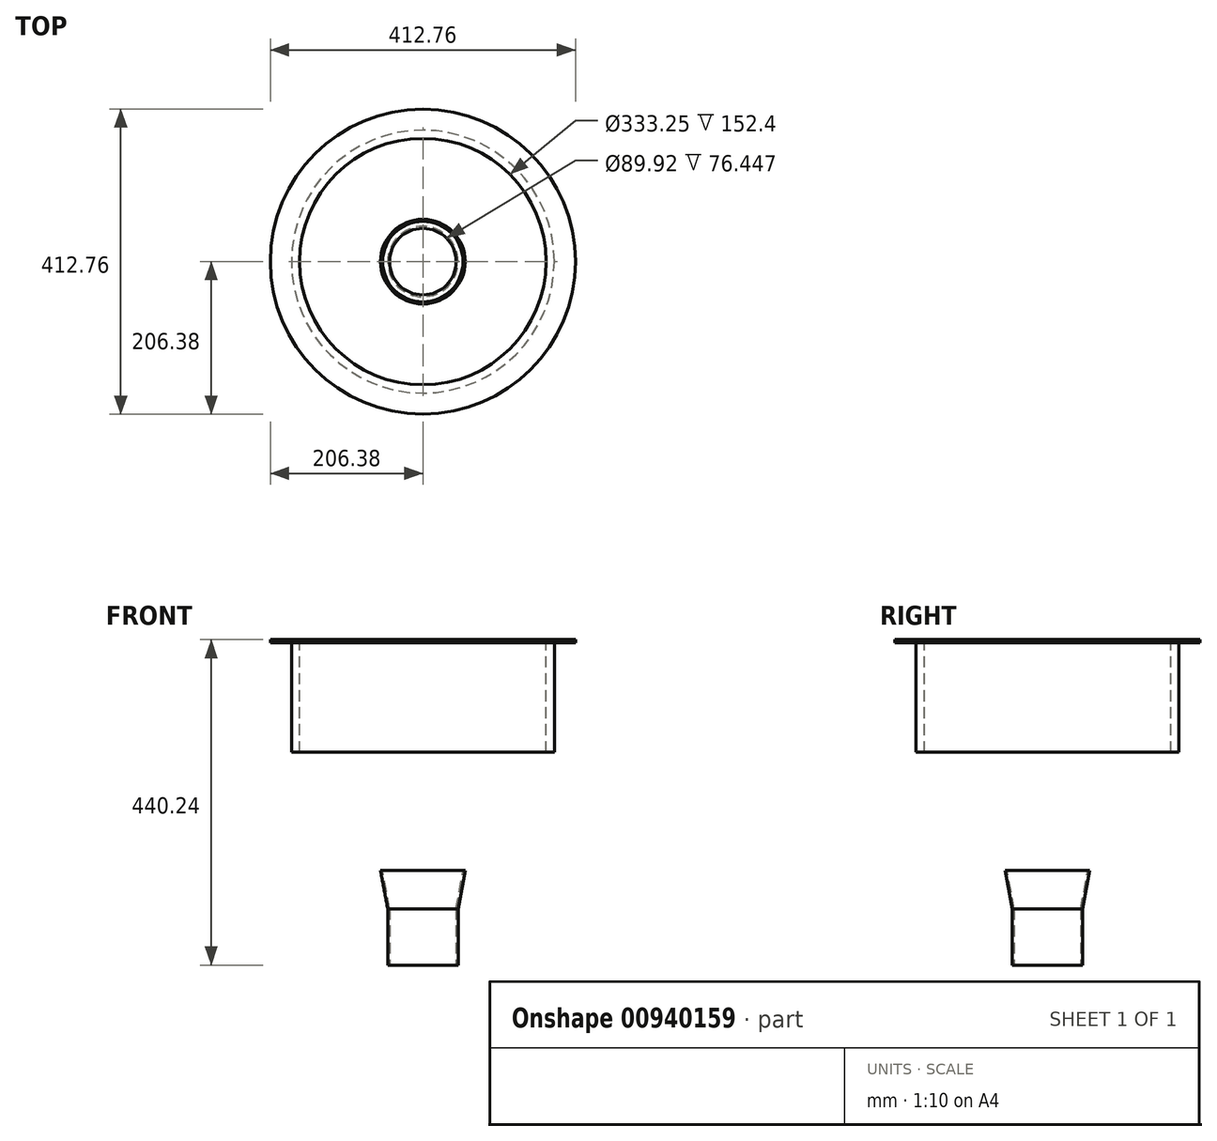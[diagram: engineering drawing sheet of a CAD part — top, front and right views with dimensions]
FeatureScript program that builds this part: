
annotation { "Feature Type Name" : "Feature", "Feature Type Description" : "" }
export const myFeature = defineFeature(function(context is Context, id is Id, definition is map)
    precondition{}
    {
        {
            var Q0;
            Q0=qCreatedBy(makeId("Top.planeOp"),FACE);
            var sketch = newSketch(context, id + "F0", { "sketchPlane" : qUnion([Q0])});
            skCircle(sketch, "E0", {"center": v(0, 0) * mm, "radius": 166.62 * mm});
            skCircle(sketch, "E1", {"center": v(0, 0) * mm, "radius": 177.8 * mm});
            skSolve(sketch);
        }
        {
            var Q0;
            Q0=qCreatedBy(makeId("Front.planeOp"),FACE);
            var sketch = newSketch(context, id + "F1", { "sketchPlane" : qUnion([Q0])});
            skLineSegment(sketch, "E2", {"start": v(0, 0) * mm, "end": v(0, -165.1) * mm, "construction": true});
            skLineSegment(sketch, "E3", {"start": v(-177.8, -71.37) * mm, "end": v(-177.8, 0) * mm});
            skLineSegment(sketch, "E4", {"start": v(-177.8, 0) * mm, "end": v(0, 0) * mm, "construction": true});
            skEllipticalArc(sketch, "E5", {});
            skLineSegment(sketch, "E6", {"start": v(0, -71.37) * mm, "end": v(-177.8, -71.37) * mm, "construction": true});
            skLineSegment(sketch, "E7.0", {"start": v(-166.62, -71.37) * mm, "end": v(-166.62, 0) * mm});
            skFitSpline(sketch, "E7.1", {"points": [v(166.62, -72.28) * mm, v(166.63, -71.37) * mm, v(166.62, -70.47) * mm, v(166.57, -69.27) * mm, v(166.47, -67.77) * mm, v(166.26, -65.98) * mm, v(165.86, -63.58) * mm, v(165.16, -60.58) * mm, v(163.96, -56.97) * mm, v(162.41, -53.34) * mm, v(160.5, -49.7) * mm, v(158.2, -46.05) * mm, v(155.54, -42.4) * mm, v(152.5, -38.78) * mm, v(149.06, -35.18) * mm, v(145.25, -31.63) * mm, v(141.06, -28.13) * mm, v(137.25, -25.27) * mm, v(134.02, -23.03) * mm, v(131.5, -21.37) * mm, v(128.9, -19.73) * mm, v(126.65, -18.39) * mm, v(124.8, -17.33) * mm, v(123.4, -16.54) * mm, v(122.2, -15.89) * mm, v(121.24, -15.37) * mm, v(120.51, -14.99) * mm, v(119.78, -14.6) * mm, v(118.8, -14.1) * mm, v(117.56, -13.46) * mm, v(116.05, -12.72) * mm, v(114.02, -11.73) * mm, v(111.43, -10.53) * mm, v(108.26, -9.13) * mm, v(105.03, -7.76) * mm, v(100.63, -6) * mm, v(94.98, -3.9) * mm, v(87.96, -1.57) * mm, v(80.73, 0.58) * mm, v(73.3, 2.55) * mm, v(65.68, 4.33) * mm, v(57.9, 5.91) * mm, v(49.96, 7.3) * mm, v(41.9, 8.48) * mm, v(33.7, 9.45) * mm, v(26.78, 10.1) * mm, v(21.2, 10.5) * mm, v(17, 10.74) * mm, v(12.77, 10.94) * mm, v(9.23, 11.05) * mm, v(6.4, 11.12) * mm, v(4.27, 11.15) * mm, v(2.5, 11.17) * mm, v(1.07, 11.17) * mm, v(0, 11.18) * mm, v(-1.07, 11.17) * mm, v(-2.5, 11.17) * mm, v(-4.27, 11.15) * mm, v(-6.4, 11.12) * mm, v(-9.23, 11.05) * mm, v(-12.77, 10.94) * mm, v(-17, 10.74) * mm, v(-21.2, 10.5) * mm, v(-26.78, 10.1) * mm, v(-33.7, 9.45) * mm, v(-41.9, 8.48) * mm, v(-49.96, 7.3) * mm, v(-57.9, 5.91) * mm, v(-65.68, 4.33) * mm, v(-73.3, 2.55) * mm, v(-80.73, 0.58) * mm, v(-87.96, -1.57) * mm, v(-94.98, -3.9) * mm, v(-100.63, -6) * mm, v(-105.03, -7.76) * mm, v(-108.26, -9.13) * mm, v(-111.43, -10.53) * mm, v(-114.02, -11.73) * mm, v(-116.05, -12.72) * mm, v(-117.56, -13.46) * mm, v(-118.8, -14.1) * mm, v(-119.78, -14.6) * mm, v(-120.51, -14.99) * mm, v(-121.24, -15.37) * mm, v(-122.2, -15.89) * mm, v(-123.4, -16.54) * mm, v(-124.8, -17.33) * mm, v(-126.65, -18.39) * mm, v(-128.9, -19.73) * mm, v(-131.5, -21.37) * mm, v(-134.02, -23.03) * mm, v(-137.25, -25.27) * mm, v(-141.06, -28.13) * mm, v(-145.25, -31.63) * mm, v(-149.06, -35.18) * mm, v(-152.5, -38.78) * mm, v(-155.54, -42.4) * mm, v(-158.2, -46.05) * mm, v(-160.5, -49.7) * mm, v(-162.41, -53.34) * mm, v(-163.96, -56.97) * mm, v(-165.16, -60.58) * mm, v(-165.86, -63.58) * mm, v(-166.26, -65.98) * mm, v(-166.47, -67.77) * mm, v(-166.57, -69.27) * mm, v(-166.62, -70.47) * mm, v(-166.63, -71.37) * mm, v(-166.62, -72.28) * mm, v(-166.57, -73.48) * mm, v(-166.47, -74.97) * mm, v(-166.26, -76.77) * mm, v(-165.86, -79.17) * mm, v(-165.16, -82.17) * mm, v(-163.96, -85.78) * mm, v(-162.41, -89.4) * mm, v(-160.5, -93.05) * mm, v(-158.2, -96.7) * mm, v(-155.54, -100.34) * mm, v(-152.5, -103.97) * mm, v(-149.06, -107.56) * mm, v(-145.25, -111.12) * mm, v(-141.06, -114.62) * mm, v(-137.25, -117.47) * mm, v(-134.02, -119.72) * mm, v(-131.5, -121.38) * mm, v(-128.9, -123.02) * mm, v(-126.65, -124.36) * mm, v(-124.8, -125.42) * mm, v(-123.4, -126.2) * mm, v(-122.2, -126.86) * mm, v(-121.24, -127.38) * mm, v(-120.51, -127.76) * mm, v(-119.78, -128.15) * mm, v(-118.8, -128.66) * mm, v(-117.56, -129.29) * mm, v(-116.05, -130.03) * mm, v(-114.02, -131.01) * mm, v(-111.43, -132.22) * mm, v(-108.26, -133.62) * mm, v(-105.03, -134.98) * mm, v(-100.63, -136.74) * mm, v(-94.98, -138.84) * mm, v(-87.96, -141.18) * mm, v(-80.73, -143.33) * mm, v(-73.3, -145.3) * mm, v(-65.68, -147.08) * mm, v(-57.9, -148.66) * mm, v(-49.96, -150.05) * mm, v(-41.9, -151.23) * mm, v(-33.7, -152.2) * mm, v(-26.78, -152.84) * mm, v(-21.2, -153.24) * mm, v(-17, -153.49) * mm, v(-12.77, -153.68) * mm, v(-9.23, -153.8) * mm, v(-6.4, -153.86) * mm, v(-4.27, -153.9) * mm, v(-2.5, -153.92) * mm, v(-1.07, -153.92) * mm, v(0, -153.92) * mm, v(1.07, -153.92) * mm, v(2.5, -153.92) * mm, v(4.27, -153.9) * mm, v(6.4, -153.86) * mm, v(9.23, -153.8) * mm, v(12.77, -153.68) * mm, v(17, -153.49) * mm, v(21.2, -153.24) * mm, v(26.78, -152.84) * mm, v(33.7, -152.2) * mm, v(41.9, -151.23) * mm, v(49.96, -150.05) * mm, v(57.9, -148.66) * mm, v(65.68, -147.08) * mm, v(73.3, -145.3) * mm, v(80.73, -143.33) * mm, v(87.96, -141.18) * mm, v(94.98, -138.84) * mm, v(100.63, -136.74) * mm, v(105.03, -134.98) * mm, v(108.26, -133.62) * mm, v(111.43, -132.22) * mm, v(114.02, -131.01) * mm, v(116.05, -130.03) * mm, v(117.56, -129.29) * mm, v(118.8, -128.66) * mm, v(119.78, -128.15) * mm, v(120.51, -127.76) * mm, v(121.24, -127.38) * mm, v(122.2, -126.86) * mm, v(123.4, -126.2) * mm, v(124.8, -125.42) * mm, v(126.65, -124.36) * mm, v(128.9, -123.02) * mm, v(131.5, -121.38) * mm, v(134.02, -119.72) * mm, v(137.25, -117.47) * mm, v(141.06, -114.62) * mm, v(145.25, -111.12) * mm, v(149.06, -107.56) * mm, v(152.5, -103.97) * mm, v(155.54, -100.34) * mm, v(158.2, -96.7) * mm, v(160.5, -93.05) * mm, v(162.41, -89.4) * mm, v(163.96, -85.78) * mm, v(165.16, -82.17) * mm, v(165.86, -79.17) * mm, v(166.26, -76.77) * mm, v(166.47, -74.97) * mm, v(166.57, -73.48) * mm, v(166.62, -72.28) * mm, v(166.63, -71.37) * mm, v(166.62, -70.47) * mm]});
            skLineSegment(sketch, "E8", {"start": v(0, -165.1) * mm, "end": v(0, -153.92) * mm});
            skLineSegment(sketch, "E9", {"start": v(-166.62, 0) * mm, "end": v(-177.8, 0) * mm});
            skLineSegment(sketch, "E10", {"start": v(-177.8, 0) * mm, "end": v(-177.8, 148.44) * mm});
            skLineSegment(sketch, "E11", {"start": v(-177.8, 148.44) * mm, "end": v(-206.38, 148.44) * mm});
            skLineSegment(sketch, "E12", {"start": v(-206.38, 148.44) * mm, "end": v(-206.38, 152.4) * mm});
            skLineSegment(sketch, "E13", {"start": v(-206.38, 152.4) * mm, "end": v(-166.62, 152.4) * mm});
            skLineSegment(sketch, "E14", {"start": v(-166.62, 152.4) * mm, "end": v(-166.62, 0) * mm});
            const initialGuessF1  = {"E5": [0, -0.071374, 1, 0, 0.1778, 0.093726, 3.141592653589793, 4.71238898038469]};
            skSetInitialGuess(sketch, initialGuessF1);
            skSolve(sketch);
        }
        {
            var Q0;
            Q0 = qSketchRegion(id + "F1", true);
            var Q1;
            Q1=sQuery(id+"F1.wireOp",EDGE,"E2");
            revolve(context, id + "F2", {"surfaceOperationType" : NewSurfaceOperationType.NEW, "entities" : qUnion([Q0]), "axis" : qUnion([Q1]), "revolveType" : RevolveType.FULL});
        }
        {
            var Q0;
            Q0=qCreatedBy(makeId("Top.planeOp"),FACE);
            var sketch = newSketch(context, id + "F3", { "sketchPlane" : qUnion([Q0])});
            skCircle(sketch, "E15", {"center": v(0, 0) * mm, "radius": 54.48 * mm});
            skSolve(sketch);
        }
        {
            var Q0;
            Q0 = qSketchRegion(id + "F3", true);
            extrude(context, id + "F4", {"entities" : qUnion([Q0]), "operationType" : NewBodyOperationType.REMOVE, "endBound" : BoundingType.THROUGH_ALL, "oppositeDirection" : true, "depth" : 25.4 * mm, "offsetDistance" : 25.4 * mm});
        }
        {
            var Q0;
            Q0=qCreatedBy(makeId("Front.planeOp"),FACE);
            var sketch = newSketch(context, id + "F5", { "sketchPlane" : qUnion([Q0])});
            skLineSegment(sketch, "E16", {"start": v(0, -287.84) * mm, "end": v(0, -160.6) * mm, "construction": true});
            skLineSegment(sketch, "E17", {"start": v(0, -287.84) * mm, "end": v(47.63, -287.84) * mm, "construction": true});
            skLineSegment(sketch, "E18", {"start": v(47.62, -211.64) * mm, "end": v(47.63, -287.84) * mm});
            skLineSegment(sketch, "E19", {"start": v(57.15, -160.6) * mm, "end": v(47.62, -211.64) * mm});
            skLineSegment(sketch, "E20", {"start": v(0, -160.6) * mm, "end": v(57.15, -160.6) * mm, "construction": true});
            skLineSegment(sketch, "E21.0", {"start": v(54.44, -160.6) * mm, "end": v(44.96, -211.4) * mm});
            skLineSegment(sketch, "E21.1", {"start": v(44.96, -211.4) * mm, "end": v(44.96, -287.84) * mm});
            skLineSegment(sketch, "E22", {"start": v(44.96, -287.84) * mm, "end": v(47.63, -287.84) * mm});
            skLineSegment(sketch, "E23", {"start": v(54.44, -160.6) * mm, "end": v(57.24, -160.11) * mm});
            skLineSegment(sketch, "E24", {"start": v(57.15, -160.6) * mm, "end": v(57.24, -160.11) * mm});
            skSolve(sketch);
        }
        {
            var Q0;
            Q0 = qSketchRegion(id + "F5", true);
            var Q1;
            Q1=sQuery(id+"F5.wireOp",EDGE,"E16");
            revolve(context, id + "F6", {"operationType" : NewBodyOperationType.ADD, "surfaceOperationType" : NewSurfaceOperationType.NEW, "entities" : qUnion([Q0]), "axis" : qUnion([Q1]), "revolveType" : RevolveType.FULL});
        }
    });
